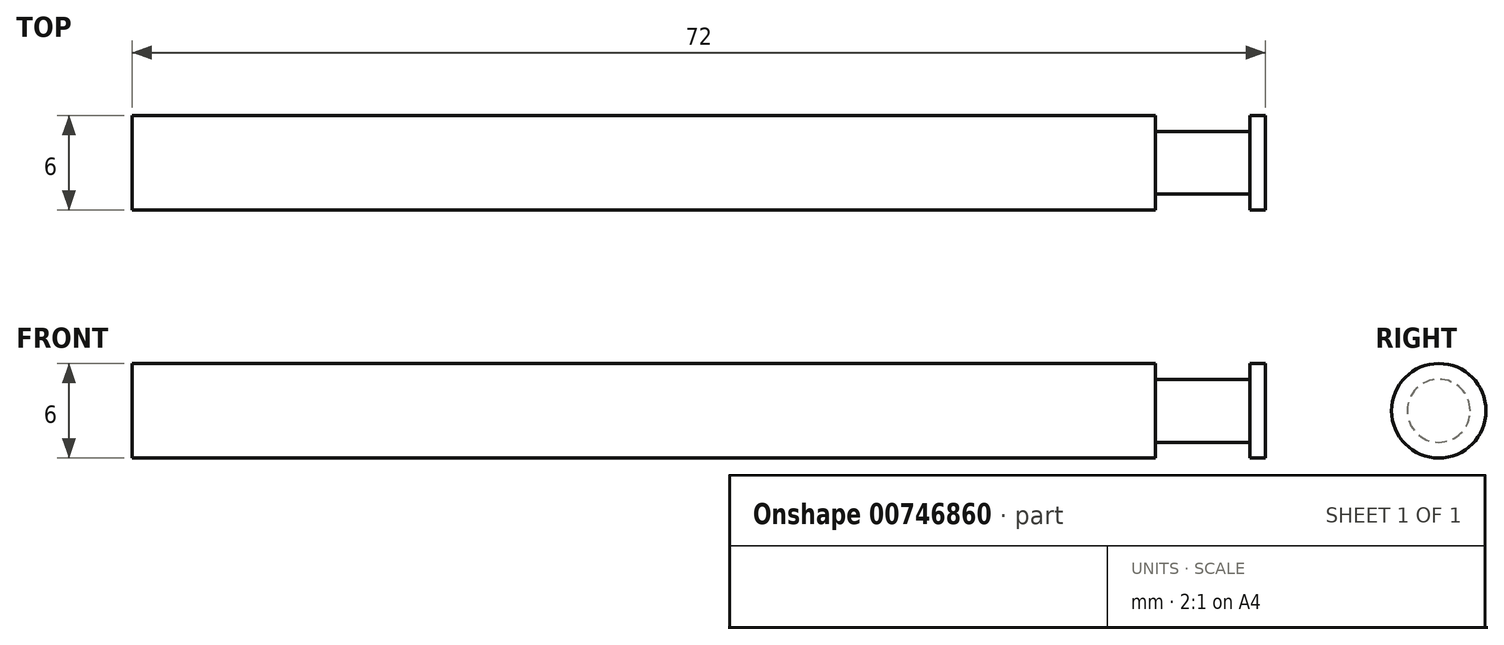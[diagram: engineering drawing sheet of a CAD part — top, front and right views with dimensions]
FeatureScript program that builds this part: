
annotation { "Feature Type Name" : "Feature", "Feature Type Description" : "" }
export const myFeature = defineFeature(function(context is Context, id is Id, definition is map)
    precondition{}
    {
        {
            var Q0;
            Q0=qCreatedBy(makeId("Right.planeOp"),FACE);
            var sketch = newSketch(context, id + "F0", { "sketchPlane" : qUnion([Q0])});
            skCircle(sketch, "E0", {"center": v(0, 0) * mm, "radius": 3 * mm});
            skSolve(sketch);
        }
        {
            var Q0;
            Q0=makeQuery(id+"F0.imprint","IMPRINT",FACE,{"disambiguationData":[TD([[makeQuery(id+"F0.imprint","IMPRINT",EDGE,{"derivedFrom":sQuery(id+"F0.wireOp",EDGE,"E0")}),1.0]])]});
            extrude(context, id + "F1", {"entities" : qUnion([Q0]), "depth" : 65 * mm, "offsetDistance" : 25 * mm});
        }
        {
            var Q0;
            Q0=makeQuery(id+"F1.opExtrude","CAP_FACE",FACE,{"disambiguationData":[OSD([sQuery(id+"F0.wireOp",EDGE,"E0")])],"isStart":false});
            var sketch = newSketch(context, id + "F2", { "sketchPlane" : qUnion([Q0])});
            skCircle(sketch, "E1", {"center": v(0, 0) * mm, "radius": 2 * mm});
            skSolve(sketch);
        }
        {
            var Q0;
            Q0=makeQuery(id+"F2.imprint","IMPRINT",FACE,{"disambiguationData":[TD([[makeQuery(id+"F2.imprint","IMPRINT",EDGE,{"derivedFrom":sQuery(id+"F2.wireOp",EDGE,"E1")}),1.0]])]});
            extrude(context, id + "F3", {"entities" : qUnion([Q0]), "operationType" : NewBodyOperationType.ADD, "depth" : 6 * mm, "offsetDistance" : 25 * mm});
        }
        {
            var Q0;
            Q0=makeQuery(id+"F3.opExtrude","CAP_FACE",FACE,{"disambiguationData":[OSD([sQuery(id+"F2.wireOp",EDGE,"E1")])],"isStart":false});
            var sketch = newSketch(context, id + "F4", { "sketchPlane" : qUnion([Q0])});
            skCircle(sketch, "E2", {"center": v(0, 0) * mm, "radius": 3 * mm});
            skSolve(sketch);
        }
        {
            var Q0;
            Q0 = qSketchRegion(id + "F4", true);
            extrude(context, id + "F5", {"entities" : qUnion([Q0]), "operationType" : NewBodyOperationType.ADD, "depth" : 1 * mm, "offsetDistance" : 25 * mm});
        }
    });
